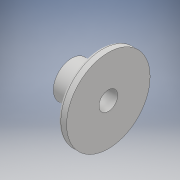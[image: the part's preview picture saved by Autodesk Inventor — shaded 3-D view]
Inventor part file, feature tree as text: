
AUTODESK INVENTOR PART (.ipt)
format: ipt  version: 2018 (Build 220112000, 112)  size: 124,416 bytes
history: native  units: mm
features: sketch x5, extrude x3, fillet x1
ambient origin geometry x8: Origin, YZ Plane, XZ Plane, XY Plane, X Axis, Y Axis, Z Axis, Center Point
bodies: Solid1 (feature_tree)
feature tree (9):
  extrude  "Extrusion1"  Depth=3.0mm TaperAngle=0.0deg
  fillet  "Fillet1"  Radius=1.0mm
  sketch  "Sketch2"  dims[d4=6.5mm d5=3.0mm d6=0.0mm]
  extrude  "Extrusion2"  Depth=3.0mm TaperAngle=0.0deg
  sketch  "Sketch4"
  sketch  "Sketch5"
  extrude  "Extrusion3"  Depth=9.75mm TaperAngle=0.0deg
  sketch  "Sketch1"  dims[d0=29.0mm d1=3.0mm d2=0.0mm d3=1.0mm]
  sketch  "Sketch3"  dims[d7=12.75mm d8=9.75mm d9=0.0mm]
